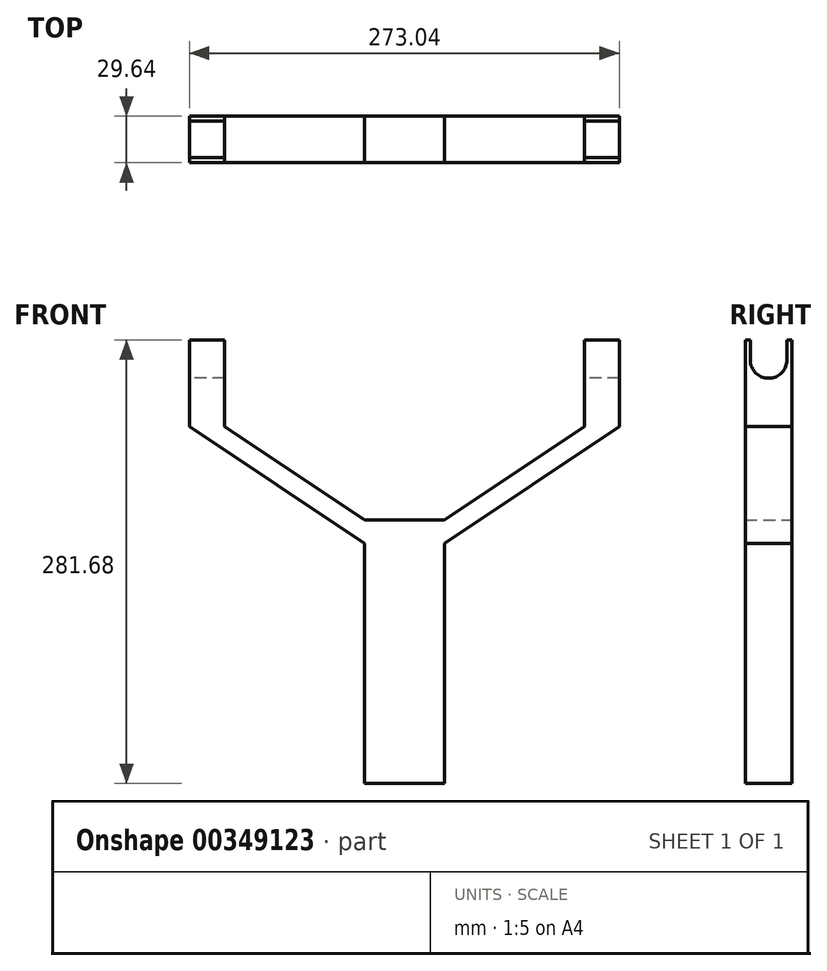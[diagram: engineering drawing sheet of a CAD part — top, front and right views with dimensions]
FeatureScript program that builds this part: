
annotation { "Feature Type Name" : "Feature", "Feature Type Description" : "" }
export const myFeature = defineFeature(function(context is Context, id is Id, definition is map)
    precondition{}
    {
        {
            var Q0;
            Q0=qCreatedBy(makeId("Front.planeOp"),FACE);
            var sketch = newSketch(context, id + "F0", { "sketchPlane" : qUnion([Q0])});
            skLineSegment(sketch, "E0", {"start": v(-25.4, -152.4) * mm, "end": v(25.4, -152.4) * mm});
            skLineSegment(sketch, "E1", {"start": v(-25.4, -152.4) * mm, "end": v(-25.4, 0) * mm});
            skLineSegment(sketch, "E2", {"start": v(25.4, -152.4) * mm, "end": v(25.4, 0) * mm});
            skLineSegment(sketch, "E3", {"start": v(-25.4, 0) * mm, "end": v(-136.52, 74.24) * mm});
            skLineSegment(sketch, "E4", {"start": v(-136.52, 74.24) * mm, "end": v(-136.52, 129.28) * mm});
            skLineSegment(sketch, "E5", {"start": v(-136.52, 129.28) * mm, "end": v(-114.3, 129.28) * mm});
            skLineSegment(sketch, "E6", {"start": v(-114.3, 129.28) * mm, "end": v(-114.3, 74.24) * mm});
            skLineSegment(sketch, "E7", {"start": v(-114.3, 74.24) * mm, "end": v(-25.4, 14.85) * mm});
            skLineSegment(sketch, "E8", {"start": v(-25.4, 14.85) * mm, "end": v(25.4, 14.85) * mm});
            skLineSegment(sketch, "E9", {"start": v(25.4, 14.85) * mm, "end": v(114.3, 74.24) * mm});
            skLineSegment(sketch, "E10", {"start": v(114.3, 74.24) * mm, "end": v(114.3, 129.28) * mm});
            skLineSegment(sketch, "E11", {"start": v(114.3, 129.28) * mm, "end": v(136.52, 129.28) * mm});
            skLineSegment(sketch, "E12", {"start": v(136.52, 129.28) * mm, "end": v(136.52, 74.24) * mm});
            skLineSegment(sketch, "E13", {"start": v(136.52, 74.24) * mm, "end": v(25.4, 0) * mm});
            skSolve(sketch);
        }
        {
            var Q0;
            Q0 = qSketchRegion(id + "F0", true);
            extrude(context, id + "F1", {"entities" : qUnion([Q0]), "depth" : 29.64 * mm});
        }
        {
            var Q0;
            Q0=makeQuery(id+"F1.opExtrude","SWEPT_FACE",FACE,{"disambiguationData":[OSD([sQuery(id+"F0.wireOp",EDGE,"E4")])]});
            var sketch = newSketch(context, id + "F2", { "sketchPlane" : qUnion([Q0])});
            skLineSegment(sketch, "E14", {"start": v(3.18, 129.28) * mm, "end": v(3.18, 116.58) * mm});
            skLineSegment(sketch, "E15", {"start": v(26.47, 129.28) * mm, "end": v(26.47, 116.58) * mm});
            skArc(sketch, "E16", {"start": v(3.18, 116.58) * mm, "mid": v(14.82, 104.94) * mm, "end": v(26.47, 116.58) * mm});
            skLineSegment(sketch, "E17", {"start": v(3.18, 129.28) * mm, "end": v(26.47, 129.28) * mm});
            skSolve(sketch);
        }
        {
            var Q0;
            Q0=makeQuery(id+"F2.imprint","IMPRINT",FACE,{"disambiguationData":[TD([[makeQuery(id+"F2.imprint","IMPRINT",EDGE,{"derivedFrom":sQuery(id+"F2.wireOp",EDGE,"E14")}),1.0]])]});
            extrude(context, id + "F3", {"entities" : qUnion([Q0]), "operationType" : NewBodyOperationType.REMOVE, "endBound" : BoundingType.THROUGH_ALL, "oppositeDirection" : true, "depth" : 25.4 * mm});
        }
    });
